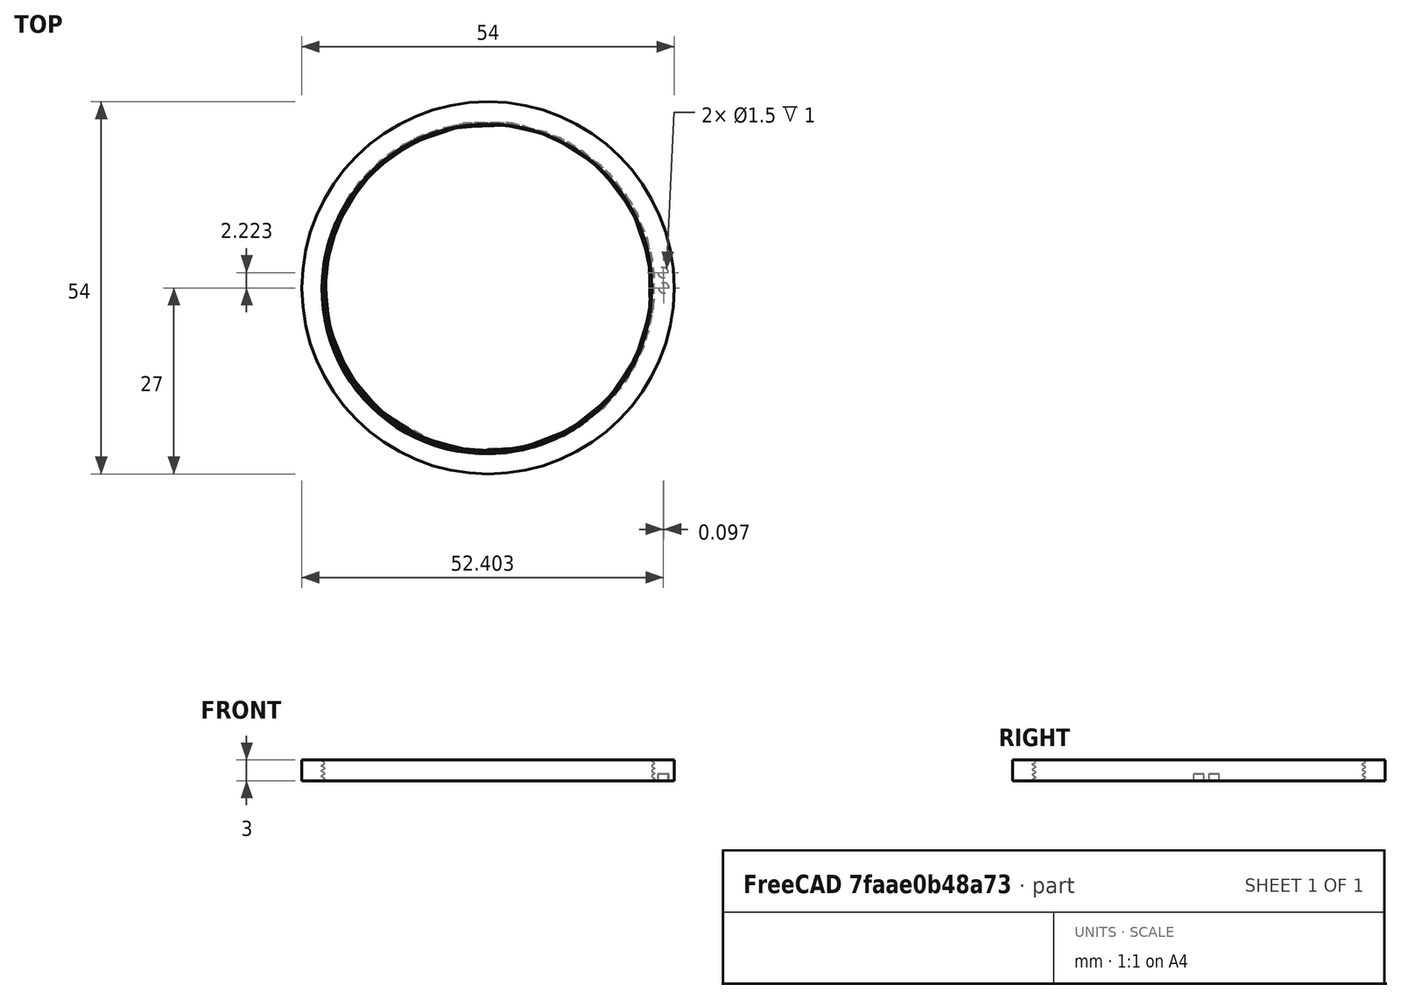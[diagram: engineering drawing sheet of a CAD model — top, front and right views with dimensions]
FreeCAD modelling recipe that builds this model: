
FCSTD DOCUMENT  (FreeCAD 2021.717R24301 +3627 (Git))
Label: tests
License: All rights reserved
LicenseURL: http://en.wikipedia.org/wiki/All_rights_reserved
objects: Part::Cylinder×2, Part::Cut×2, Part::Part2DObjectPython×1, PartDesign::AdditiveHelix×1, PartDesign::Body×1, Part::FeaturePython×1
note: 10 computed .brp shape members not serialized (recipe doc carries the construction recipe); baked Part::Feature solids carry a one-line shape summary decoded from their .brp

FEATURE [Part::Part2DObjectPython] VThreadProfile001  # Draft 2D object (typed FeaturePython)
  Area = 1799.11
  Closed = true
  Continuity = C3
  Instructions = Expand this with the ... button to view instructions | Sweep this object along a helix of the same pitch to produce your thread. | It is recommended to make the helix in the ThreadProfile workbench. | If there is an active Body the ThreadProfile object will be put into it.,If not it can be dragged and dropped into the body later. | If there is an active Body when the helix is made there will be made a ShapeBinder for it | For internal threads you will need to cut the Sweep object out of a cylinder, or if using Part Design sweep it as a Subtractive Pipe. | Always use Frenet mode | I have provided some presets, but it is possible there could be some errors.  Double check for mission critical applications. | Also, the tolerances might be different from what you wish to have.  I believe the internal minor diameters are all minimum and the external are all maximum.
  InternalOrExternal = 0
  MakeFace = true
  MinorDiameter = 47.5
  Parameterization = 1
  Pitch = 0.75
  Points = (719) [(23.7491,0.207543,0),(23.7464,0.415071,0),(23.7418,0.622567,0),(23.7355,0.830015,0),(23.7273,1.0374,0),(23.7174,1.24471,0),(23.7056,1.45192,0),+712 more]
  Presets = 0
  Quality = 1
  ThreadCount = 10
  Version = 1.69
  external_data = [-0.00235387,-0.00461052,-0.00677828,-0.00886428,-0.0108747,-0.0128149,-0.0146895,-0.0165028,-0.0182584,-0.0199597,-0.0216095,-0.0232106,-0.0247653,-0.0262759,-0.0277444,-0.0291725,-0.0305621,-0.0319145,-0.0332313,-0.0345138,-0.0357632,+698 more]
  internal_data = [0,0,0,0,0,0,0,0,0,0,0,0,0,0,0,0,0,0,0,0,0,0,0,0,0,0,0,0,0,0,0,0,0,0,0,0,0,0,0,0,0,0,0,0,0,0,0,0,0,0,0,0,0,0,0,0,0,0,0,0,0,0,0,0,0,0,0,0,0,0,0,0,0,0,0,0,0,0,0,0,0,0,0,0,0,0,0,0,0,0,0,0,0,0,0,0,0,0,0,0,0,0,0,0,0,0,0,0,0,0,0,0,0,0,0,0,0,0,0,0,+599 more]
  preset_names = <blob: 3959 chars omitted>
  presets_data = [0,0,0,2.20878,24.1173,24.6888,0.25,0.693,0.729,0.25,0.793,0.829,0.25,0.893,0.929,0.3,1.032,1.075,0.35,1.171,1.221,0.35,1.371,1.421,0.4,1.509,1.567,0.45,1.648,1.713,0.45,1.948,2.013,0.5,2.387,2.459,0.6,2.764,2.85,0.7,3.141,3.242,0.75,3.58,+712 more]
FEATURE [PartDesign::AdditiveHelix] AdditiveHelix001
  Angle = 0
  Axis = (-3e-16,3e-16,1)
  Base = (0,0,0)
  ClaimChildren = false
  Fit = 0
  FitJoin = 0
  HasBeenEdited = true
  Height = 6
  InnerFit = 0
  InnerFitJoin = 0
  LeftHanded = false
  Mode = 0
  NewSolid = false
  Outside = false
  Pitch = 0.75
  Profile = -> VThreadProfile001
  ReferenceAxis = -> Z_Axis001
  Refine = true
  Suppress = false
  Turns = 3
  _ProfileBasedVersion = 1
FEATURE [PartDesign::Body] Body001
  AutoGroupSolids = false
  ExportMode = 0
  Group = -> [VThreadProfile001,AdditiveHelix001]
  Origin = -> Origin001
  Tip = -> AdditiveHelix001
  _ExportChildren = -> [AdditiveHelix001]
  _GroupVersion = 1
FEATURE [Part::Cylinder] Cylinder
  Angle = 360
  AttacherType = Attacher::AttachEngine3D
  Height = 3
  Radius = 27
FEATURE [Part::Cut] Cut
  Base = -> Cylinder
  Refine = true
  Tool = -> Body001
FEATURE [Part::Cylinder] Cylinder001
  Angle = 360
  AttacherType = Attacher::AttachEngine3D
  Height = 1
  Placement = pos=(25.5,0,0) rot=(0,0,1;0rad)
  Radius = 0.75
FEATURE [Part::FeaturePython] Array  # Draft array (typed FeaturePython)
  Angle = 5
  ArrayType = 1
  Axis = (0,0,1)
  Base = -> Cylinder001
  Center = (0,0,0)
  Fuse = false
  IntervalAxis = (0,0,0)
  IntervalX = (50,0,0)
  IntervalY = (0,50,0)
  IntervalZ = (0,0,50)
  NumberCircles = 3
  NumberPolar = 2
  NumberX = 2
  NumberY = 2
  NumberZ = 1
  RadialDistance = 50
  Symmetry = 1
  TangentialDistance = 25
FEATURE [Part::Cut] Cut001
  Base = -> Cut
  Refine = true
  Tool = -> Array
